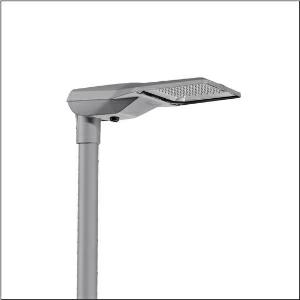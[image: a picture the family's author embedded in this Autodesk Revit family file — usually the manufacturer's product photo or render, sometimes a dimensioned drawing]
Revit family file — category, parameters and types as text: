
# Revit family: streetlight_sl_21_iq_midi___st1_0ab_5xe3m31u08nb_407f
name_source: partatom
category: Lighting Fixtures
units: mm (PartAtom-declared; Revit-internal decimal feet)

## family parameters
Cut with Voids When Loaded = No
Host = Face
Light Source = No
Part Type = Normal
Room Calculation Point = No
Round Connector Dimension = Use Diameter
Shared = No

## types (1)
- --- (1 x LED, 18970 lm, 136.6 W, 3000K)
    Apparent Load = 137 VA
    CIE Flux Codes = 40 74 97 100 100
    Color Rendering = 70
    Color Temperature = 3000K
    Default Elevation = 1800 mm
    Description = Streetlight SL 21 iQ midi, mast luminaire, primary light control with lens, of PMMA, primary optical cover: cover, of toughened safety glass, transparent, light distribution: ST1.0aB, light emission: direct distribution, primary light characteristic: asymmetric, installation type: post-top, side-entry, LED, High Power LED, rated luminous flux: 18.970lm, luminous efficacy: 139lm/W, light colour: 730, colour temperature: 3000K, control: presetting dimming logarithmic, Street-Remote, Auto-Match, Temp-Guard, Lumen-Switch, Night-Set, Smart-Wire, Light-Fading, Desk-Remote (wireless, voltage-free reading and setting of iQ features in the workshop via application-optimized NFC function/RFID function), optimised constant luminous flux control (CLO 2.0), mains connection: 230..240V, AC, 50/60Hz, start of lifetime: 137W, end of service life: 144W, reduction: 61W, luminaire housing, of diecast aluminium, powder-coated, Siteco® metallic grey (DB 702S), corrosivity category C5 mid according to DIN EN ISO 12944, please order mast flange separately, inclination adjustable: 0°, 5°, 10°, 15°, sealing non-destructively replaceable, multi-level sealing system, length: 644mm, width: 335mm, height: 110mm, mast flange for spigot size: 42mm (side-entry): 5XC10008XM4, 60/48mm (side-entry/post-top): 5XC10108XM2, 76/60mm (side-entry/post-top): 5XC10108XM1, Smart Interface below, protection rating (complete): IP66, insulation class (complete): insulation class II (safety insulation), certification: CE, ENEC, ENEC+, VDE, impact resistance: IK09, permissible operating ambient temperature for outdoor applications: -40..+50°C, standard-compliant lighting for roads and squares, packaging unit: 1 piece

Light Distribution: ST1.0aB
    Height = 111 mm
    Lamp = 1 x LED
    Lamp Light Flux = 18970 lm
    Lamp Power = 136.6 W
    Lamp count = 1
    Length = 644 mm
    Luminous efficacy = 139 lm/W
    Manufacturer = Siteco
    ModVariant = No
    Model = 5XE3M31U08NB
    Number of Poles = 1
    OnlyDefault = Yes
    Power Factor = 1
    Product Name = Streetlight SL 21 iQ midi | ST1.0aB
    Product group = mast luminaire | pylon top
    ProductGroupID = 6100
    Protection Class = Protection class II
    Protection Degree = IP 66
    RLX_Detail_Level = 1
    RLX_Emergency_Light_Flux = 0 lm
    RLX_Emergency_Type = 0
    RLX_Emergency_Type_DB = No
    RlxData = <blob elided: 92377 chars, md5=e565a429>
    Socket = socket
    Standby Power = 0 W
    System Light Flux = 18970 lm
    System Power = 137 W
    Type Comments = factory setting: luminous flux: 100 % | dim-lin: 254 | 733 mA
    Type Image = l_1004300.jpg
    URL = http://relux.com
    VarID = @adj_042217
    Voltage = 0 V
    Weight = 0.00 kg
    Width = 336 mm

## geometry (parser evidence)
native form markers: Blend x4, Sweep x11
no freeform markers — native parametric forms only
